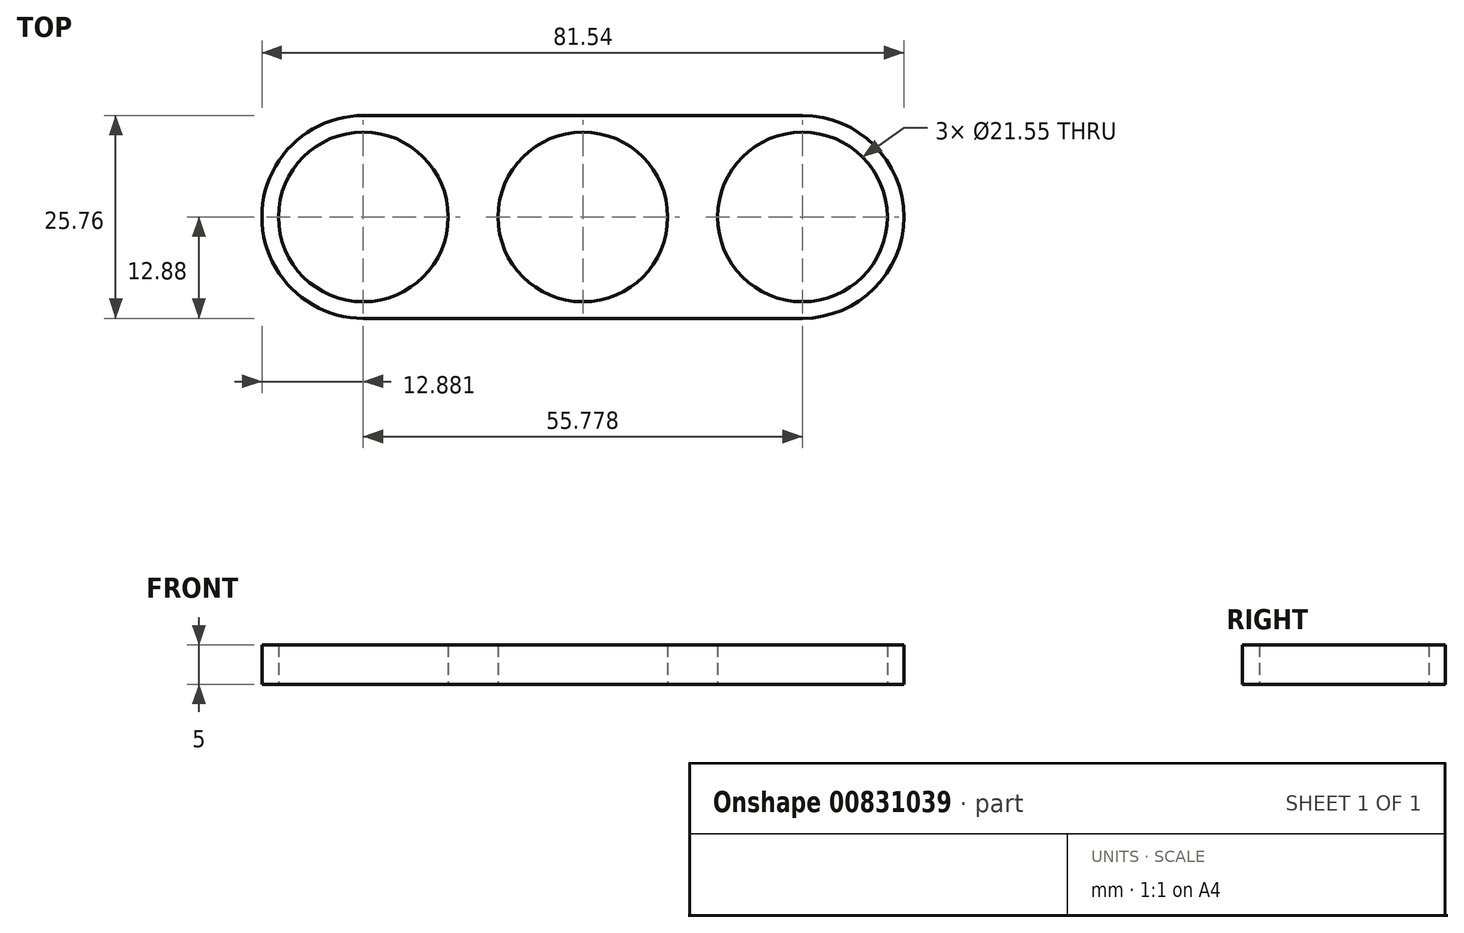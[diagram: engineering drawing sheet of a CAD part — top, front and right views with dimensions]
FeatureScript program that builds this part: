
annotation { "Feature Type Name" : "Feature", "Feature Type Description" : "" }
export const myFeature = defineFeature(function(context is Context, id is Id, definition is map)
    precondition{}
    {
        {
            var Q0;
            Q0=qCreatedBy(makeId("Top.planeOp"),FACE);
            var sketch = newSketch(context, id + "F0", { "sketchPlane" : qUnion([Q0])});
            skCircle(sketch, "E0", {"center": v(-27.89, 0) * mm, "radius": 10.78 * mm});
            skCircle(sketch, "E1", {"center": v(0, 0) * mm, "radius": 10.78 * mm});
            skCircle(sketch, "E2", {"center": v(0, 0) * mm, "radius": 12.88 * mm});
            skCircle(sketch, "E3", {"center": v(-27.89, 0) * mm, "radius": 12.88 * mm});
            skCircle(sketch, "E4.MirrorC", {"center": v(27.89, 0) * mm, "radius": 10.78 * mm});
            skCircle(sketch, "E5.MirrorC", {"center": v(27.89, 0) * mm, "radius": 12.88 * mm});
            skLineSegment(sketch, "E6", {"start": v(-27.85, 12.88) * mm, "end": v(27.89, 12.88) * mm});
            skLineSegment(sketch, "E7", {"start": v(-27.9, -12.88) * mm, "end": v(27.89, -12.88) * mm});
            skSolve(sketch);
        }
        {
            var Q0;
            Q0 = qSketchRegion(id + "F0", true);
            extrude(context, id + "F1", {"entities" : qUnion([Q0]), "depth" : 5 * mm, "offsetDistance" : 25 * mm});
        }
    });
